# Revit family: BuzziSpace - BuzziJet
name_source: partatom
category: Lighting Fixtures
units: mm (PartAtom-declared; Revit-internal decimal feet)

## family parameters
Always vertical = Yes
Cut with Voids When Loaded = No
Host = Ceiling
Light Source = Yes
OmniClass Number = 23.80.70.11
OmniClass Title = Luminaries for Internal Lighting
Part Type = Normal
Room Calculation Point = No
Round Connector Dimension = Use Diameter
Shared = No

## types (4) — shared parameters
Color Filter = 16777215
Dimming Lamp Color Temperature Shift = <None>
Light Source Symbol Size = 61 cm
Manufacturer = BuzziSpace
Model = BuzziJet
Shade = <By Category>
URL = https://www.buzzi.space

## per-type parameters (varying)
| type | Cord Position | Shade Diameter | Shade Height | Support Mid Radius | Support Radius |
| Small | 20 cm | 80 cm | 23 cm | 35 cm | 39 cm |
| Medium | 20 cm | 80 cm | 45 cm | 35 cm | 39 cm |
| XL | 30 cm | 120 cm | 53 cm | 35 cm | 39 cm |
| XXL | 45 cm | 150 cm | 60 cm | 70 cm | 74 cm |

## geometry (parser evidence)
native form markers: Sweep x5
no freeform markers — native parametric forms only
